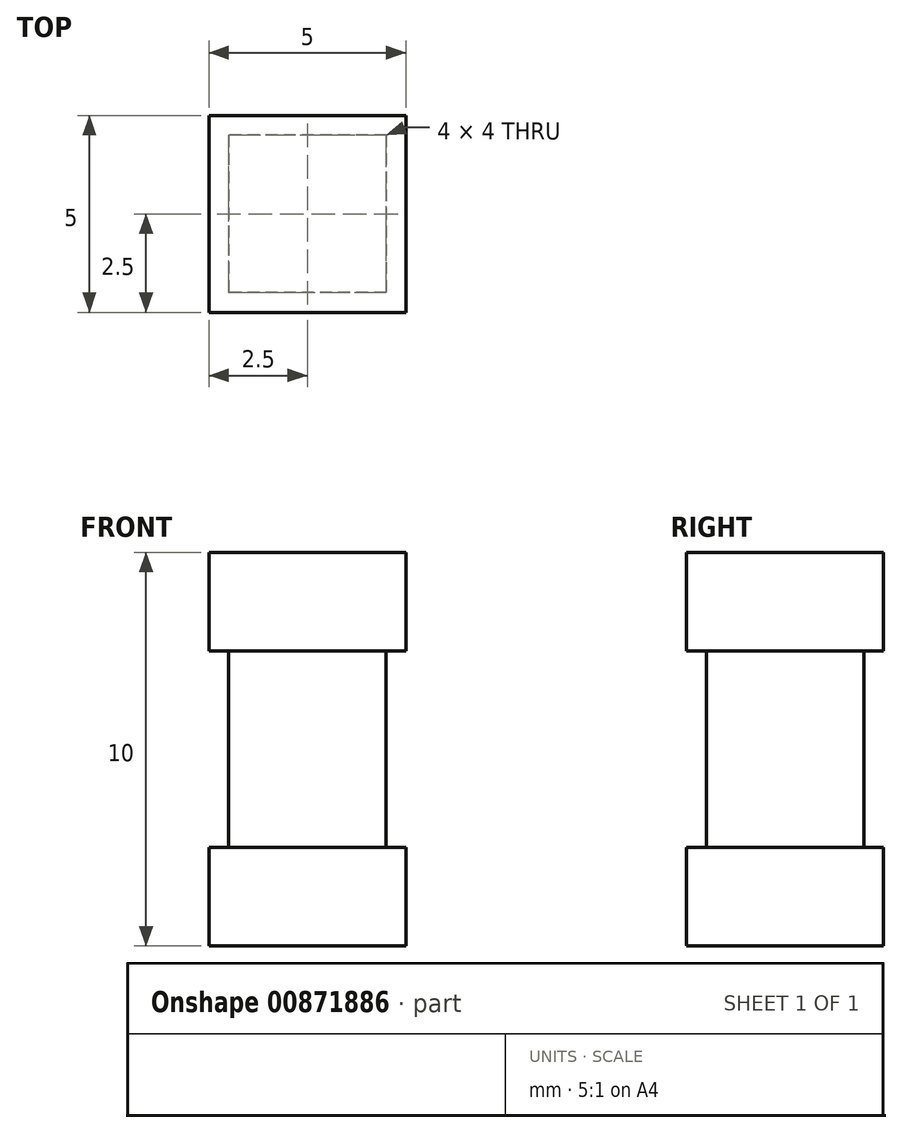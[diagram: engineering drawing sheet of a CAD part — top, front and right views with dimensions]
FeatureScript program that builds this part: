
annotation { "Feature Type Name" : "Feature", "Feature Type Description" : "" }
export const myFeature = defineFeature(function(context is Context, id is Id, definition is map)
    precondition{}
    {
        {
            var Q0;
            Q0=qCreatedBy(makeId("Top.planeOp"),FACE);
            var sketch = newSketch(context, id + "F0", { "sketchPlane" : qUnion([Q0])});
            skLineSegment(sketch, "E0.bottom", {"start": v(2.5, 2.5) * mm, "end": v(-2.5, 2.5) * mm});
            skLineSegment(sketch, "E0.top", {"start": v(2.5, -2.5) * mm, "end": v(-2.5, -2.5) * mm});
            skLineSegment(sketch, "E0.left", {"start": v(2.5, 2.5) * mm, "end": v(2.5, -2.5) * mm});
            skLineSegment(sketch, "E0.right", {"start": v(-2.5, 2.5) * mm, "end": v(-2.5, -2.5) * mm});
            skPoint(sketch, "E0.middle", {"position": v(0, 0) * mm});
            skSolve(sketch);
        }
        {
            var Q0;
            Q0=makeQuery(id+"F0.imprint","IMPRINT",FACE,{"disambiguationData":[TD([[makeQuery(id+"F0.imprint","IMPRINT",EDGE,{"derivedFrom":sQuery(id+"F0.wireOp",EDGE,"E0.bottom")}),1.0]])]});
            extrude(context, id + "F1", {"entities" : qUnion([Q0]), "depth" : 10 * mm, "offsetDistance" : 25.4 * mm});
        }
        {
            var Q0;
            Q0=qCreatedBy(makeId("Top.planeOp"),FACE);
            var sketch = newSketch(context, id + "F2", { "sketchPlane" : qUnion([Q0])});
            skLineSegment(sketch, "E1.bottom", {"start": v(2, 2) * mm, "end": v(-2, 2) * mm});
            skLineSegment(sketch, "E1.top", {"start": v(2, -2) * mm, "end": v(-2, -2) * mm});
            skLineSegment(sketch, "E1.left", {"start": v(2, 2) * mm, "end": v(2, -2) * mm});
            skLineSegment(sketch, "E1.right", {"start": v(-2, 2) * mm, "end": v(-2, -2) * mm});
            skPoint(sketch, "E1.middle", {"position": v(0, 0) * mm});
            skSolve(sketch);
        }
        {
            var Q0;
            Q0=qCreatedBy(makeId("Top.planeOp"),FACE);
            var sketch = newSketch(context, id + "F3", { "sketchPlane" : qUnion([Q0])});
            skLineSegment(sketch, "E2.bottom", {"start": v(2.5, 2.5) * mm, "end": v(-2.5, 2.5) * mm});
            skLineSegment(sketch, "E2.top", {"start": v(2.5, -2.5) * mm, "end": v(-2.5, -2.5) * mm});
            skLineSegment(sketch, "E2.left", {"start": v(2.5, 2.5) * mm, "end": v(2.5, -2.5) * mm});
            skLineSegment(sketch, "E2.right", {"start": v(-2.5, 2.5) * mm, "end": v(-2.5, -2.5) * mm});
            skPoint(sketch, "E2.middle", {"position": v(0, 0) * mm});
            skSolve(sketch);
        }
        {
            var Q0;
            Q0 = qSketchRegion(id + "F3", true);
            extrude(context, id + "F4", {"entities" : qUnion([Q0]), "depth" : 5 * mm, "offsetDistance" : 25.4 * mm});
        }
        {
            var Q0;
            Q0 = qSketchRegion(id + "F2", true);
            extrude(context, id + "F5", {"entities" : qUnion([Q0]), "depth" : 5 * mm, "offsetDistance" : 25.4 * mm});
        }
        {
            var Q0;
            Q0=makeQuery(id+"F5.opExtrude","SWEPT_BODY",BODY,{"disambiguationData":[OSD([sQuery(id+"F2.wireOp",EDGE,"E1.bottom"),sQuery(id+"F2.wireOp",EDGE,"E1.top"),sQuery(id+"F2.wireOp",EDGE,"E1.left"),sQuery(id+"F2.wireOp",EDGE,"E1.right")])]});
            var Q1;
            Q1=makeQuery(id+"F4.opExtrude","SWEPT_BODY",BODY,{"disambiguationData":[OSD([sQuery(id+"F3.wireOp",EDGE,"E2.bottom"),sQuery(id+"F3.wireOp",EDGE,"E2.top"),sQuery(id+"F3.wireOp",EDGE,"E2.left"),sQuery(id+"F3.wireOp",EDGE,"E2.right")])]});
            booleanBodies(context, id + "F6", {"operationType" : BooleanOperationType.SUBTRACTION, "tools" : qUnion([Q0]), "targets" : qUnion([Q1])});
        }
        {
            var Q0;
            Q0=makeQuery(id+"F4.opExtrude","SWEPT_BODY",BODY,{"disambiguationData":[OSD([sQuery(id+"F3.wireOp",EDGE,"E2.bottom"),sQuery(id+"F3.wireOp",EDGE,"E2.top"),sQuery(id+"F3.wireOp",EDGE,"E2.left"),sQuery(id+"F3.wireOp",EDGE,"E2.right")])]});
            var Q1;
            Q1=makeQuery(id+"F6.opBoolean","COPY",EDGE,{"derivedFrom":makeQuery(id+"F5.opExtrude","SWEPT_EDGE",EDGE,{"disambiguationData":[OSD([sQuery(id+"F2.wireOp",EDGE,"E1.bottom"),sQuery(id+"F2.wireOp",EDGE,"E1.right")])]})});
            transform(context, id + "F7", {"entities" : qUnion([Q0]), "transformType" : TransformType.TRANSLATION_DISTANCE, "transformDirection" : qUnion([Q1]), "distance" : 2.5 * mm, "oppositeDirection" : true, "makeCopy" : false});
        }
        {
            var Q0;
            Q0=makeQuery(id+"F4.opExtrude","SWEPT_BODY",BODY,{"disambiguationData":[OSD([sQuery(id+"F3.wireOp",EDGE,"E2.bottom"),sQuery(id+"F3.wireOp",EDGE,"E2.top"),sQuery(id+"F3.wireOp",EDGE,"E2.left"),sQuery(id+"F3.wireOp",EDGE,"E2.right")])]});
            var Q1;
            Q1=makeQuery(id+"F1.opExtrude","SWEPT_BODY",BODY,{"disambiguationData":[OSD([sQuery(id+"F0.wireOp",EDGE,"E0.bottom"),sQuery(id+"F0.wireOp",EDGE,"E0.top"),sQuery(id+"F0.wireOp",EDGE,"E0.left"),sQuery(id+"F0.wireOp",EDGE,"E0.right")])]});
            booleanBodies(context, id + "F8", {"operationType" : BooleanOperationType.SUBTRACTION, "tools" : qUnion([Q0]), "targets" : qUnion([Q1])});
        }
    });
